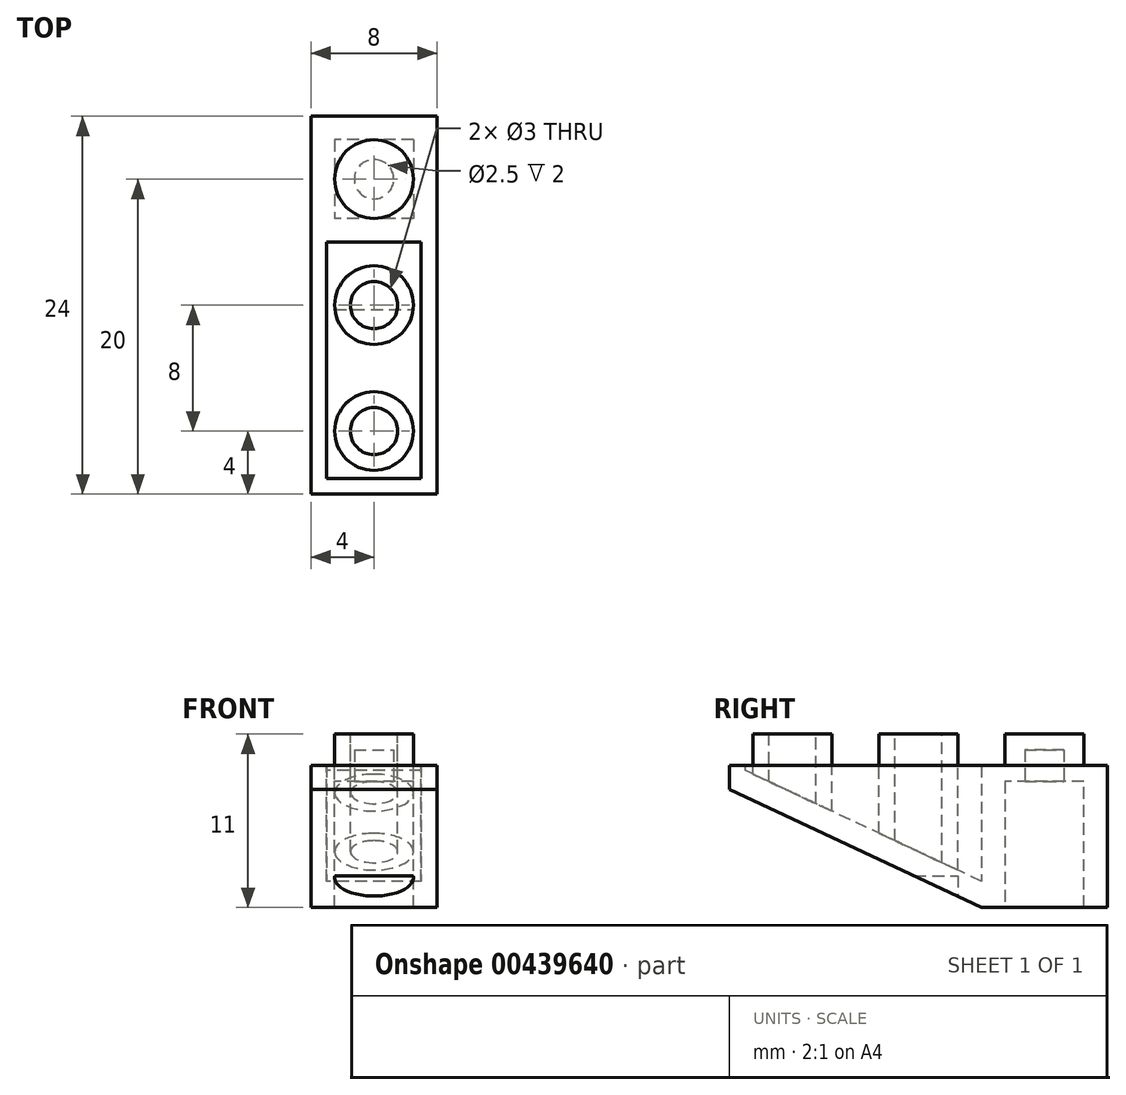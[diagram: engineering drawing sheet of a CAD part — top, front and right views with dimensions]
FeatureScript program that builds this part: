
annotation { "Feature Type Name" : "Feature", "Feature Type Description" : "" }
export const myFeature = defineFeature(function(context is Context, id is Id, definition is map)
    precondition{}
    {
        {
            var Q0;
            Q0=qCreatedBy(makeId("Right.planeOp"),FACE);
            var sketch = newSketch(context, id + "F0", { "sketchPlane" : qUnion([Q0])});
            skLineSegment(sketch, "E0.bottom", {"start": v(0, 0) * mm, "end": v(-8, 0) * mm});
            skLineSegment(sketch, "E0.top", {"start": v(0, 9) * mm, "end": v(-24, 9) * mm});
            skLineSegment(sketch, "E0.left", {"start": v(0, 0) * mm, "end": v(0, 9) * mm});
            skLineSegment(sketch, "E0.right", {"start": v(-24, 7.5) * mm, "end": v(-24, 9) * mm});
            skLineSegment(sketch, "E1", {"start": v(-8, 0) * mm, "end": v(-24, 7.5) * mm});
            skSolve(sketch);
        }
        {
            var Q0;
            Q0 = qSketchRegion(id + "F0", true);
            extrude(context, id + "F1", {"entities" : qUnion([Q0]), "depth" : 4 * mm});
        }
        {
            var Q0;
            Q0=makeQuery(id+"F1.opExtrude","CAP_FACE",FACE,{"disambiguationData":[OSD([sQuery(id+"F0.wireOp",EDGE,"E0.bottom"),sQuery(id+"F0.wireOp",EDGE,"E0.top"),sQuery(id+"F0.wireOp",EDGE,"E0.left"),sQuery(id+"F0.wireOp",EDGE,"E0.right"),sQuery(id+"F0.wireOp",EDGE,"E1")])],"isStart":true});
            var sketch = newSketch(context, id + "F2", { "sketchPlane" : qUnion([Q0])});
            skLineSegment(sketch, "E2", {"start": v(8, 9) * mm, "end": v(8, 1.66) * mm});
            skLineSegment(sketch, "E3.0", {"start": v(8, 1.66) * mm, "end": v(23, 8.69) * mm});
            skLineSegment(sketch, "E4.0", {"start": v(23, 8.69) * mm, "end": v(23, 9) * mm});
            skLineSegment(sketch, "E5", {"start": v(8, 9) * mm, "end": v(23, 9) * mm});
            skLineSegment(sketch, "E6", {"start": v(1.5, 0) * mm, "end": v(1.5, 8) * mm});
            skLineSegment(sketch, "E7", {"start": v(1.5, 8) * mm, "end": v(6.5, 8) * mm});
            skLineSegment(sketch, "E8", {"start": v(6.5, 8) * mm, "end": v(6.5, 0) * mm});
            skLineSegment(sketch, "E9", {"start": v(6.5, 0) * mm, "end": v(1.5, 0) * mm});
            skSolve(sketch);
        }
        {
            var Q0;
            Q0=makeQuery(id+"F2.imprint","IMPRINT",FACE,{"disambiguationData":[TD([[makeQuery(id+"F2.imprint","IMPRINT",EDGE,{"derivedFrom":sQuery(id+"F2.wireOp",EDGE,"E2")}),1.0]])]});
            extrude(context, id + "F3", {"entities" : qUnion([Q0]), "operationType" : NewBodyOperationType.REMOVE, "oppositeDirection" : true, "depth" : 3 * mm});
        }
        {
            var Q0;
            Q0=makeQuery(id+"F2.imprint","IMPRINT",FACE,{"disambiguationData":[TD([[makeQuery(id+"F2.imprint","IMPRINT",EDGE,{"derivedFrom":sQuery(id+"F2.wireOp",EDGE,"E6")}),-1.0]])]});
            extrude(context, id + "F4", {"entities" : qUnion([Q0]), "operationType" : NewBodyOperationType.REMOVE, "oppositeDirection" : true, "depth" : 2.5 * mm});
        }
        {
            var Q0;
            Q0=makeQuery(id+"F1.opExtrude","SWEPT_BODY",BODY,{"disambiguationData":[OSD([sQuery(id+"F0.wireOp",EDGE,"E0.bottom"),sQuery(id+"F0.wireOp",EDGE,"E0.top"),sQuery(id+"F0.wireOp",EDGE,"E0.left"),sQuery(id+"F0.wireOp",EDGE,"E0.right"),sQuery(id+"F0.wireOp",EDGE,"E1")])]});
            var Q1;
            Q1=makeQuery(id+"F1.opExtrude","CAP_FACE",FACE,{"disambiguationData":[OSD([sQuery(id+"F0.wireOp",EDGE,"E0.bottom"),sQuery(id+"F0.wireOp",EDGE,"E0.top"),sQuery(id+"F0.wireOp",EDGE,"E0.left"),sQuery(id+"F0.wireOp",EDGE,"E0.right"),sQuery(id+"F0.wireOp",EDGE,"E1")])],"isStart":true});
            mirror(context, id + "F5", {"operationType" : NewBodyOperationType.ADD, "entities" : qUnion([Q0]), "mirrorPlane" : qUnion([Q1])});
        }
        {
            var Q0;
            {var subQ0=makeQuery(id+"F1.opExtrude","SWEPT_FACE",FACE,{"disambiguationData":[OSD([sQuery(id+"F0.wireOp",EDGE,"E0.top")])]});Q0=makeQuery(id+"F5.boolean.opBoolean","MERGE",FACE,{"derivedFrom":[subQ0,makeQuery(id+"F5.opPattern","COPY",FACE,{"derivedFrom":subQ0,"instanceName":"1"})]});}
            var sketch = newSketch(context, id + "F6", { "sketchPlane" : qUnion([Q0])});
            skCircle(sketch, "E10", {"center": v(0, -4) * mm, "radius": 2.5 * mm});
            skSolve(sketch);
        }
        {
            var Q0;
            Q0=makeQuery(id+"F6.imprint","IMPRINT",FACE,{"disambiguationData":[TD([[makeQuery(id+"F6.imprint","IMPRINT",EDGE,{"derivedFrom":sQuery(id+"F6.wireOp",EDGE,"E10")}),1.0]])]});
            extrude(context, id + "F7", {"entities" : qUnion([Q0]), "operationType" : NewBodyOperationType.ADD, "depth" : 2 * mm});
        }
        {
            var Q0;
            {var subQ0=makeQuery(id+"F1.opExtrude","SWEPT_FACE",FACE,{"disambiguationData":[OSD([sQuery(id+"F0.wireOp",EDGE,"E0.bottom")])]});Q0=makeQuery(id+"F5.boolean.opBoolean","MERGE",FACE,{"derivedFrom":[subQ0,makeQuery(id+"F5.opPattern","COPY",FACE,{"derivedFrom":subQ0,"instanceName":"1"})]});}
            var sketch = newSketch(context, id + "F8", { "sketchPlane" : qUnion([Q0])});
            skCircle(sketch, "E11", {"center": v(0, 4) * mm, "radius": 1.25 * mm});
            skSolve(sketch);
        }
        {
            var Q0;
            Q0=makeQuery(id+"F8.imprint","IMPRINT",FACE,{"disambiguationData":[TD([[makeQuery(id+"F8.imprint","IMPRINT",EDGE,{"derivedFrom":sQuery(id+"F8.wireOp",EDGE,"E11")}),1.0]])]});
            extrude(context, id + "F9", {"entities" : qUnion([Q0]), "operationType" : NewBodyOperationType.REMOVE, "oppositeDirection" : true, "depth" : 10 * mm});
        }
        {
            var Q0;
            Q0=makeQuery(id+"F7.opExtrude","CAP_FACE",FACE,{"disambiguationData":[OSD([sQuery(id+"F6.wireOp",EDGE,"E10")])],"isStart":false});
            var sketch = newSketch(context, id + "F10", { "sketchPlane" : qUnion([Q0])});
            skCircle(sketch, "E12", {"center": v(0, -12) * mm, "radius": 2.5 * mm});
            skCircle(sketch, "E13", {"center": v(0, -12) * mm, "radius": 1.5 * mm});
            skCircle(sketch, "E14.0.1.0", {"center": v(0, -20) * mm, "radius": 1.5 * mm});
            skCircle(sketch, "E14.0.1.1", {"center": v(0, -20) * mm, "radius": 2.5 * mm});
            skLineSegment(sketch, "E14.direction1", {"start": v(0, -12) * mm, "end": v(25, -12) * mm, "construction": true});
            skLineSegment(sketch, "E14.direction2", {"start": v(0, -12) * mm, "end": v(0, -20) * mm, "construction": true});
            skSolve(sketch);
        }
        {
            var Q0;
            Q0=makeQuery(id+"F10.imprint","IMPRINT",FACE,{"disambiguationData":[TD([[makeQuery(id+"F10.imprint","IMPRINT",EDGE,{"derivedFrom":sQuery(id+"F10.wireOp",EDGE,"E12")}),1.0]])]});
            var Q1;
            Q1=makeQuery(id+"F10.imprint","IMPRINT",FACE,{"disambiguationData":[TD([[makeQuery(id+"F10.imprint","IMPRINT",EDGE,{"derivedFrom":sQuery(id+"F10.wireOp",EDGE,"E14.0.1.0")}),-1.0]])]});
            extrude(context, id + "F11", {"entities" : qUnion([Q0, Q1]), "operationType" : NewBodyOperationType.ADD, "endBound" : BoundingType.UP_TO_NEXT, "oppositeDirection" : true, "depth" : 25 * mm});
        }
        {
            var Q0;
            {var subQ0=makeQuery(id+"F1.opExtrude","SWEPT_FACE",FACE,{"disambiguationData":[OSD([sQuery(id+"F0.wireOp",EDGE,"E0.bottom")])]});Q0=makeQuery(id+"F5.boolean.opBoolean","MERGE",FACE,{"derivedFrom":[subQ0,makeQuery(id+"F5.opPattern","COPY",FACE,{"derivedFrom":subQ0,"instanceName":"1"})]});}
            var sketch = newSketch(context, id + "F12", { "sketchPlane" : qUnion([Q0])});
            skCircle(sketch, "E15", {"center": v(0, 12) * mm, "radius": 2.5 * mm});
            skSolve(sketch);
        }
        {
            var Q0;
            Q0 = qSketchRegion(id + "F12", true);
            extrude(context, id + "F13", {"entities" : qUnion([Q0]), "operationType" : NewBodyOperationType.REMOVE, "oppositeDirection" : true, "depth" : 2 * mm});
        }
    });
